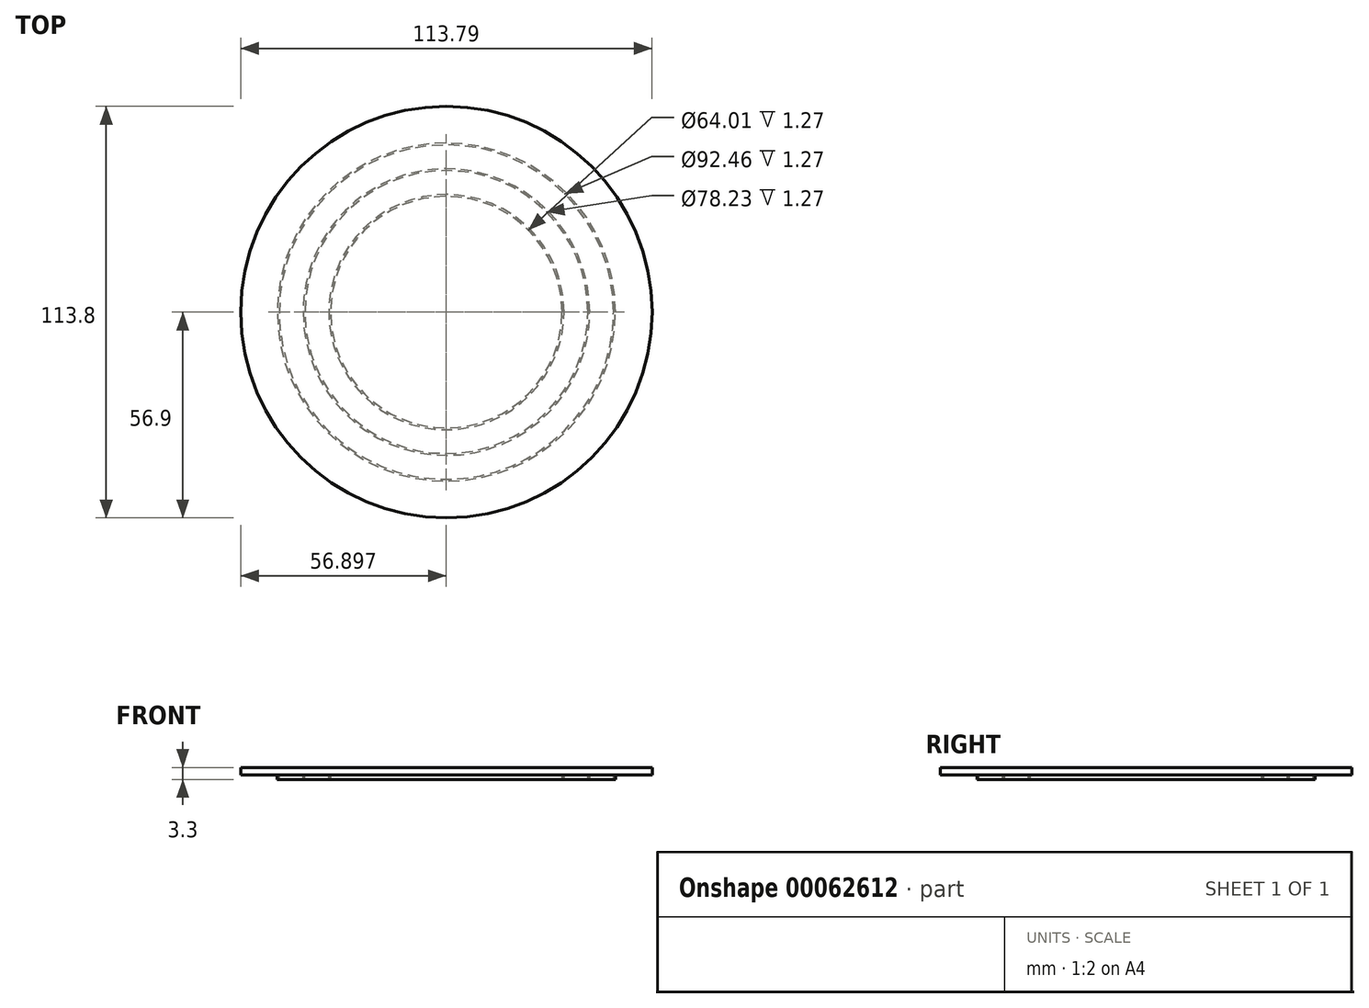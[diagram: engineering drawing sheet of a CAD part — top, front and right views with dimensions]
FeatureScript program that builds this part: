
annotation { "Feature Type Name" : "Feature", "Feature Type Description" : "" }
export const myFeature = defineFeature(function(context is Context, id is Id, definition is map)
    precondition{}
    {
        {
            var Q0;
            Q0=qCreatedBy(makeId("Front.planeOp"),FACE);
            var sketch = newSketch(context, id + "F0", { "sketchPlane" : qUnion([Q0])});
            skLineSegment(sketch, "E0.bottom", {"start": v(-35.48, 4.3) * mm, "end": v(21.42, 4.3) * mm});
            skLineSegment(sketch, "E0.top", {"start": v(-35.48, 2.28) * mm, "end": v(-25.32, 2.28) * mm});
            skLineSegment(sketch, "E0.left", {"start": v(-35.48, 4.3) * mm, "end": v(-35.48, 2.28) * mm});
            skLineSegment(sketch, "E0.right", {"start": v(21.42, 4.3) * mm, "end": v(21.42, 2.28) * mm});
            skPoint(sketch, "E1", {"position": v(-10.59, 2.28) * mm});
            skLineSegment(sketch, "E2.bottom", {"start": v(-10.59, 2.28) * mm, "end": v(-11.1, 2.28) * mm});
            skLineSegment(sketch, "E2.top", {"start": v(-10.59, 1) * mm, "end": v(-11.1, 1) * mm});
            skLineSegment(sketch, "E2.left", {"start": v(-10.59, 2.28) * mm, "end": v(-10.59, 1) * mm});
            skLineSegment(sketch, "E2.right", {"start": v(-11.1, 2.28) * mm, "end": v(-11.1, 1) * mm});
            skLineSegment(sketch, "E3.bottom", {"start": v(-18.2, 2.28) * mm, "end": v(-17.7, 2.28) * mm});
            skLineSegment(sketch, "E3.top", {"start": v(-18.2, 1) * mm, "end": v(-17.7, 1) * mm});
            skLineSegment(sketch, "E3.left", {"start": v(-18.2, 2.28) * mm, "end": v(-18.2, 1) * mm});
            skLineSegment(sketch, "E3.right", {"start": v(-17.7, 2.28) * mm, "end": v(-17.7, 1) * mm});
            skLineSegment(sketch, "E4.bottom", {"start": v(-25.32, 2.28) * mm, "end": v(-24.81, 2.28) * mm});
            skLineSegment(sketch, "E4.top", {"start": v(-25.32, 1) * mm, "end": v(-24.81, 1) * mm});
            skLineSegment(sketch, "E4.left", {"start": v(-25.32, 2.28) * mm, "end": v(-25.32, 1) * mm});
            skLineSegment(sketch, "E4.right", {"start": v(-24.81, 2.28) * mm, "end": v(-24.81, 1) * mm});
            skLineSegment(sketch, "E5", {"start": v(-24.81, 2.28) * mm, "end": v(-18.2, 2.28) * mm});
            skLineSegment(sketch, "E6", {"start": v(-17.7, 2.28) * mm, "end": v(-11.1, 2.28) * mm});
            skLineSegment(sketch, "E7", {"start": v(-10.59, 2.28) * mm, "end": v(21.42, 2.28) * mm});
            skLineSegment(sketch, "E8", {"start": v(-11.1, 2.28) * mm, "end": v(-11.1, 2.28) * mm});
            skLineSegment(sketch, "E9", {"start": v(-11.1, 2.28) * mm, "end": v(-10.59, 2.28) * mm});
            skSolve(sketch);
        }
        {
            var Q0;
            Q0 = qSketchRegion(id + "F0", true);
            var Q1;
            Q1=sQuery(id+"F0.wireOp",EDGE,"E0.right");
            revolve(context, id + "F1", {"entities" : qUnion([Q0]), "axis" : qUnion([Q1]), "revolveType" : RevolveType.FULL});
        }
    });
